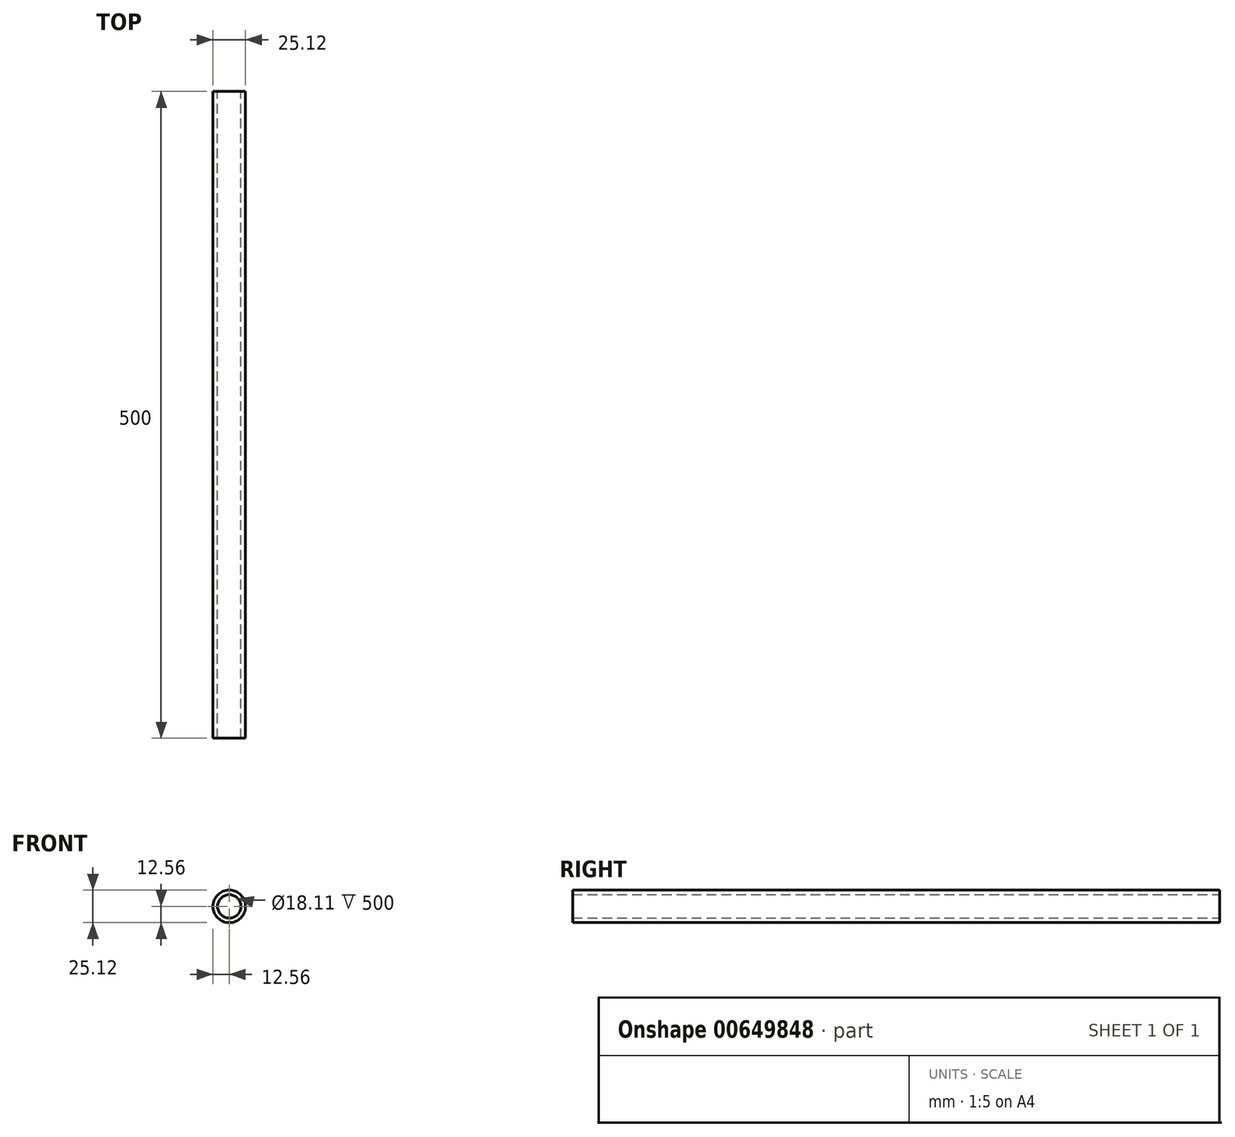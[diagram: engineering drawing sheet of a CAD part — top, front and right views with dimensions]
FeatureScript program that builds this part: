
annotation { "Feature Type Name" : "Feature", "Feature Type Description" : "" }
export const myFeature = defineFeature(function(context is Context, id is Id, definition is map)
    precondition{}
    {
        {
            var Q0;
            Q0=qCreatedBy(makeId("Front.planeOp"),FACE);
            var sketch = newSketch(context, id + "F0", { "sketchPlane" : qUnion([Q0])});
            skCircle(sketch, "E0", {"center": v(0, 0) * mm, "radius": 12.56 * mm});
            skCircle(sketch, "E1.0", {"center": v(0, 0) * mm, "radius": 9.06 * mm});
            skSolve(sketch);
        }
        {
            var Q0;
            Q0 = qSketchRegion(id + "F0", true);
            extrude(context, id + "F1", {"entities" : qUnion([Q0]), "depth" : 250 * mm, "offsetDistance" : 25 * mm, "hasSecondDirection" : true, "secondDirectionOppositeDirection" : true, "secondDirectionDepth" : 250 * mm});
        }
    });
